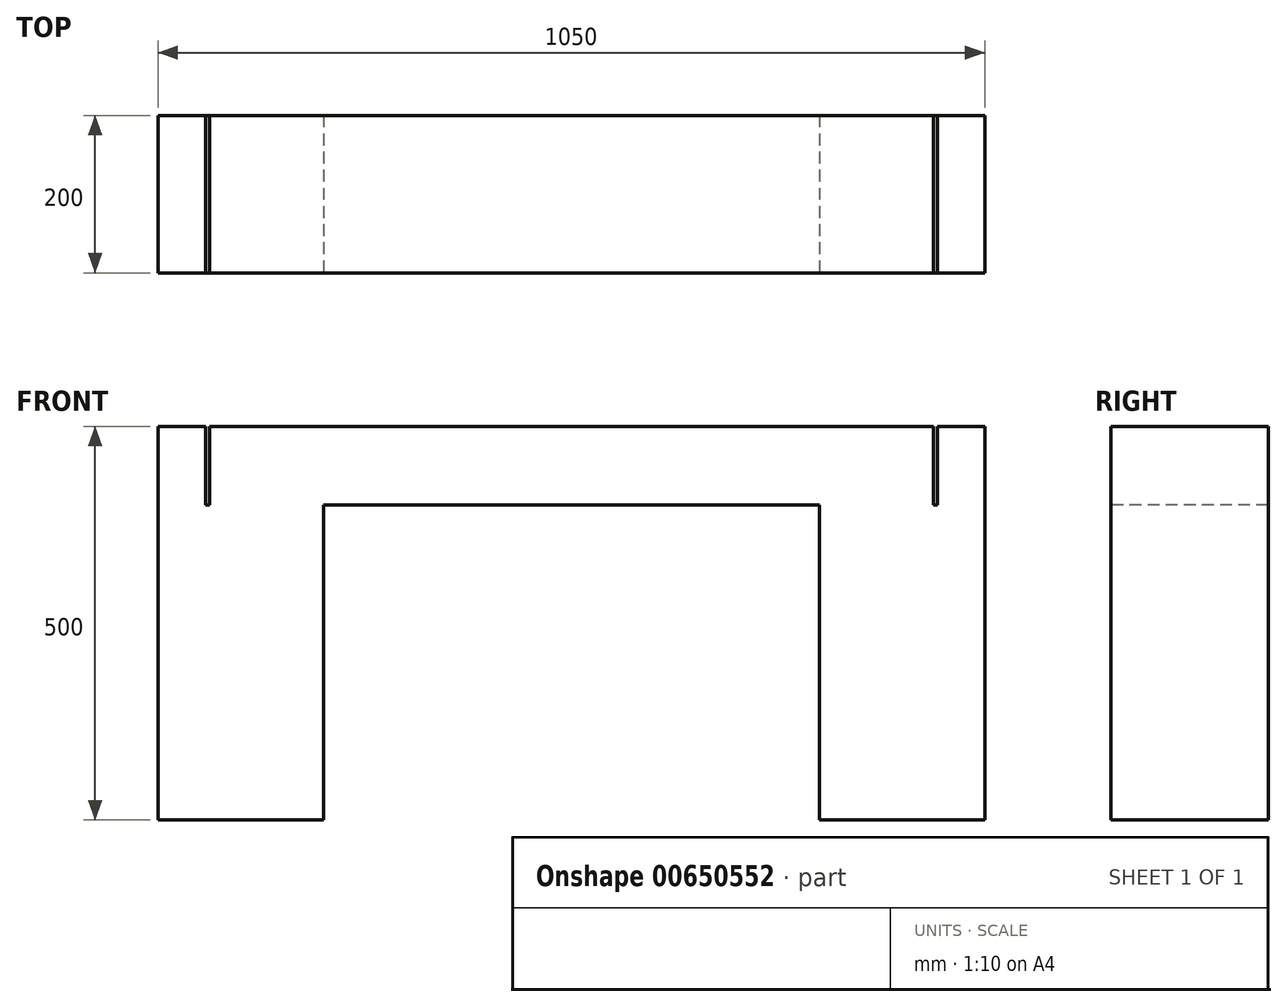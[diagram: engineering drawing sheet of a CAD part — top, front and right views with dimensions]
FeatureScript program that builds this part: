
annotation { "Feature Type Name" : "Feature", "Feature Type Description" : "" }
export const myFeature = defineFeature(function(context is Context, id is Id, definition is map)
    precondition{}
    {
        {
            var Q0;
            Q0=qCreatedBy(makeId("Top.planeOp"),FACE);
            var sketch = newSketch(context, id + "F0", { "sketchPlane" : qUnion([Q0])});
            skLineSegment(sketch, "E0.bottom", {"start": v(-525, 0) * mm, "end": v(-315, 0) * mm});
            skLineSegment(sketch, "E0.top", {"start": v(-525, -200) * mm, "end": v(-315, -200) * mm});
            skLineSegment(sketch, "E0.left", {"start": v(-525, 0) * mm, "end": v(-525, -200) * mm});
            skLineSegment(sketch, "E0.right", {"start": v(-315, 0) * mm, "end": v(-315, -200) * mm});
            skLineSegment(sketch, "E1", {"start": v(0, 160.52) * mm, "end": v(0, -168) * mm, "construction": true});
            skLineSegment(sketch, "E2.MirrorCS", {"start": v(525, -200) * mm, "end": v(315, -200) * mm});
            skLineSegment(sketch, "E3.MirrorCS", {"start": v(315, 0) * mm, "end": v(315, -200) * mm});
            skLineSegment(sketch, "E4.MirrorCS", {"start": v(525, 0) * mm, "end": v(315, 0) * mm});
            skLineSegment(sketch, "E5.MirrorCS", {"start": v(525, 0) * mm, "end": v(525, -200) * mm});
            skSolve(sketch);
        }
        {
            var Q0;
            Q0 = qSketchRegion(id + "F0", true);
            extrude(context, id + "F1", {"entities" : qUnion([Q0]), "depth" : 400 * mm, "offsetDistance" : 25 * mm});
        }
        {
            var Q0;
            Q0=makeQuery(id+"F1.opExtrude","CAP_FACE",FACE,{"disambiguationData":[OSD([sQuery(id+"F0.wireOp",EDGE,"E0.bottom"),sQuery(id+"F0.wireOp",EDGE,"E0.top"),sQuery(id+"F0.wireOp",EDGE,"E0.left"),sQuery(id+"F0.wireOp",EDGE,"E0.right")])],"isStart":false});
            var sketch = newSketch(context, id + "F2", { "sketchPlane" : qUnion([Q0])});
            skPoint(sketch, "E6.oppositeSnap0", {"position": v(-420, -200) * mm});
            skLineSegment(sketch, "E6.bottom", {"start": v(-460, 0) * mm, "end": v(460, 0) * mm});
            skLineSegment(sketch, "E6.top", {"start": v(-460, -200) * mm, "end": v(460, -200) * mm});
            skLineSegment(sketch, "E6.left", {"start": v(-460, 0) * mm, "end": v(-460, -200) * mm});
            skLineSegment(sketch, "E6.right", {"start": v(460, 0) * mm, "end": v(460, -200) * mm});
            skSolve(sketch);
        }
        {
            var Q0;
            Q0 = qSketchRegion(id + "F2", true);
            extrude(context, id + "F3", {"entities" : qUnion([Q0]), "operationType" : NewBodyOperationType.ADD, "depth" : 100 * mm, "offsetDistance" : 25 * mm});
        }
        {
            var Q0;
            Q0=makeQuery(id+"F1.opExtrude","CAP_FACE",FACE,{"disambiguationData":[OSD([sQuery(id+"F0.wireOp",EDGE,"E0.bottom"),sQuery(id+"F0.wireOp",EDGE,"E0.top"),sQuery(id+"F0.wireOp",EDGE,"E0.left"),sQuery(id+"F0.wireOp",EDGE,"E0.right")])],"isStart":false});
            var sketch = newSketch(context, id + "F4", { "sketchPlane" : qUnion([Q0])});
            skLineSegment(sketch, "E7.bottom", {"start": v(-525, 0) * mm, "end": v(-465, 0) * mm});
            skLineSegment(sketch, "E7.top", {"start": v(-525, -200) * mm, "end": v(-465, -200) * mm});
            skLineSegment(sketch, "E7.left", {"start": v(-525, 0) * mm, "end": v(-525, -200) * mm});
            skLineSegment(sketch, "E7.right", {"start": v(-465, 0) * mm, "end": v(-465, -200) * mm});
            skLineSegment(sketch, "E8.bottom", {"start": v(525, -200) * mm, "end": v(465, -200) * mm});
            skLineSegment(sketch, "E8.top", {"start": v(525, 0) * mm, "end": v(465, 0) * mm});
            skLineSegment(sketch, "E8.left", {"start": v(525, -200) * mm, "end": v(525, 0) * mm});
            skLineSegment(sketch, "E8.right", {"start": v(465, -200) * mm, "end": v(465, 0) * mm});
            skSolve(sketch);
        }
        {
            var Q0;
            Q0 = qSketchRegion(id + "F4", true);
            extrude(context, id + "F5", {"entities" : qUnion([Q0]), "operationType" : NewBodyOperationType.ADD, "depth" : 100 * mm, "offsetDistance" : 25 * mm});
        }
    });
